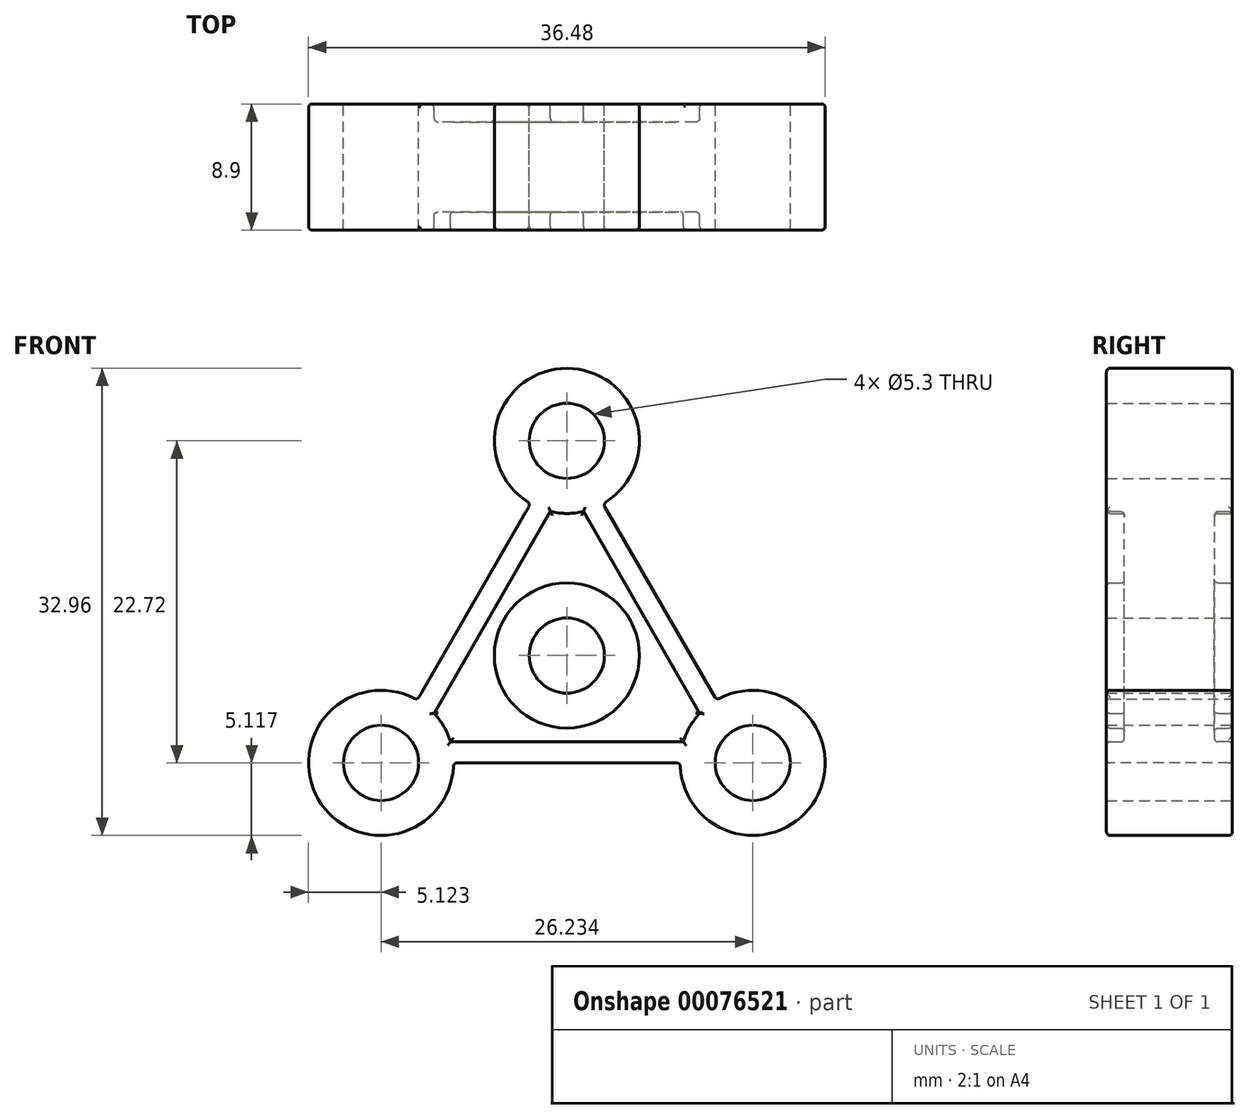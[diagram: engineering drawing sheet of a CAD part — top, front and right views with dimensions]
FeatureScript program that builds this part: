
annotation { "Feature Type Name" : "Feature", "Feature Type Description" : "" }
export const myFeature = defineFeature(function(context is Context, id is Id, definition is map)
    precondition{}
    {
        {
            var Q0;
            Q0=qCreatedBy(makeId("Front.planeOp"),FACE);
            var sketch = newSketch(context, id + "F0", { "sketchPlane" : qUnion([Q0])});
            skCircle(sketch, "E0.cCircle", {"center": v(0, 0) * mm, "radius": 7.57 * mm, "construction": true});
            skLineSegment(sketch, "E0.0", {"start": v(12.23, -7.57) * mm, "end": v(-12.23, -7.57) * mm});
            skLineSegment(sketch, "E0.1", {"start": v(-12.67, -6.8) * mm, "end": v(-0.44, 14.38) * mm});
            skLineSegment(sketch, "E0.2", {"start": v(0.44, 14.38) * mm, "end": v(12.67, -6.8) * mm});
            skPoint(sketch, "E0.0.midPoint", {"position": v(0, -7.57) * mm});
            skLineSegment(sketch, "E1", {"start": v(-0.44, 14.38) * mm, "end": v(0.44, 14.38) * mm});
            skLineSegment(sketch, "E2", {"start": v(12.67, -6.8) * mm, "end": v(12.23, -7.57) * mm});
            skLineSegment(sketch, "E3", {"start": v(-12.23, -7.57) * mm, "end": v(-12.67, -6.8) * mm});
            skPoint(sketch, "E4.orphan", {"position": v(0, 15.15) * mm});
            skPoint(sketch, "E5.orphan", {"position": v(-13.12, -7.57) * mm});
            skPoint(sketch, "E6.orphan", {"position": v(13.12, -7.57) * mm});
            skLineSegment(sketch, "E7", {"start": v(0, 0) * mm, "end": v(13.12, -7.57) * mm, "construction": true});
            skLineSegment(sketch, "E8", {"start": v(0, 0) * mm, "end": v(0, 15.15) * mm, "construction": true});
            skLineSegment(sketch, "E9", {"start": v(0, 0) * mm, "end": v(-13.12, -7.57) * mm, "construction": true});
            skSolve(sketch);
        }
        {
            var Q0;
            Q0=qCreatedBy(makeId("Front.planeOp"),FACE);
            var sketch = newSketch(context, id + "F2", { "sketchPlane" : qUnion([Q0])});
            skLineSegment(sketch, "E10.0.0", {"start": v(-12.23, -7.57) * mm, "end": v(12.23, -7.57) * mm});
            skLineSegment(sketch, "E10.0.1", {"start": v(12.23, -7.57) * mm, "end": v(12.67, -6.8) * mm});
            skLineSegment(sketch, "E10.0.2", {"start": v(12.67, -6.8) * mm, "end": v(0.44, 14.38) * mm});
            skLineSegment(sketch, "E10.0.3", {"start": v(0.44, 14.38) * mm, "end": v(-0.44, 14.38) * mm});
            skLineSegment(sketch, "E10.0.4", {"start": v(-0.44, 14.38) * mm, "end": v(-12.67, -6.8) * mm});
            skLineSegment(sketch, "E10.0.5", {"start": v(-12.67, -6.8) * mm, "end": v(-12.23, -7.57) * mm});
            skPoint(sketch, "E11.0", {"position": v(0, 0) * mm});
            skPoint(sketch, "E12.0", {"position": v(0, 15.15) * mm});
            skPoint(sketch, "E13.0", {"position": v(-13.12, -7.57) * mm});
            skPoint(sketch, "E14.0", {"position": v(13.12, -7.57) * mm});
            skPoint(sketch, "E15.0", {"position": v(0, -7.57) * mm});
            skCircle(sketch, "E16", {"center": v(0, 15.15) * mm, "radius": 5.12 * mm});
            skCircle(sketch, "E17", {"center": v(-13.12, -7.57) * mm, "radius": 5.12 * mm});
            skCircle(sketch, "E18", {"center": v(13.12, -7.57) * mm, "radius": 5.12 * mm});
            skCircle(sketch, "E19", {"center": v(0, 0) * mm, "radius": 2.65 * mm});
            skCircle(sketch, "E20", {"center": v(13.12, -7.57) * mm, "radius": 2.65 * mm});
            skCircle(sketch, "E21", {"center": v(0, 15.15) * mm, "radius": 2.65 * mm});
            skCircle(sketch, "E22", {"center": v(-13.12, -7.57) * mm, "radius": 2.65 * mm});
            skCircle(sketch, "E23", {"center": v(0, 0) * mm, "radius": 5.12 * mm});
            skCircle(sketch, "E24.cCircle", {"center": v(0, 0) * mm, "radius": 6.09 * mm, "construction": true});
            skLineSegment(sketch, "E24.0", {"start": v(10.54, -6.09) * mm, "end": v(-10.54, -6.09) * mm});
            skLineSegment(sketch, "E24.1", {"start": v(-10.54, -6.09) * mm, "end": v(0, 12.17) * mm});
            skLineSegment(sketch, "E24.2", {"start": v(0, 12.17) * mm, "end": v(10.54, -6.09) * mm});
            skPoint(sketch, "E24.0.midPoint", {"position": v(0, -6.09) * mm});
            skSolve(sketch);
        }
        {
            var Q0;
            Q0 = qSketchRegion(id + "F2", true);
            var Q1;
            Q1=makeQuery(id+"F2.imprint","IMPRINT",FACE,{"disambiguationData":[TD([[makeQuery(id+"F2.imprint","IMPRINT",EDGE,{"derivedFrom":sQuery(id+"F2.wireOp",EDGE,"E19")}),-1.0]])]});
            var Q2;
            {var subQ0=sQuery(id+"F2.wireOp",EDGE,"E24.2");var subQ1=sQuery(id+"F2.wireOp",EDGE,"E18");var subQ2=makeQuery(id+"F2.imprint","INTERSECT",VERTEX,{"derivedFrom":[subQ1,subQ0]});Q2=makeQuery(id+"F2.imprint","IMPRINT",FACE,{"disambiguationData":[TD([[makeQuery(id+"F2.imprint","IMPRINT",EDGE,{"disambiguationData":[TD([[subQ2,-1.0]])],"derivedFrom":subQ1}),1.0]])]});}
            var Q3;
            {var subQ0=sQuery(id+"F2.wireOp",EDGE,"E24.1");var subQ1=sQuery(id+"F2.wireOp",EDGE,"E16");var subQ2=makeQuery(id+"F2.imprint","INTERSECT",VERTEX,{"derivedFrom":[subQ1,subQ0]});Q3=makeQuery(id+"F2.imprint","IMPRINT",FACE,{"disambiguationData":[TD([[makeQuery(id+"F2.imprint","IMPRINT",EDGE,{"disambiguationData":[TD([[subQ2,-1.0]])],"derivedFrom":subQ1}),1.0]])]});}
            var Q4;
            Q4=makeQuery(id+"F2.imprint","IMPRINT",FACE,{"disambiguationData":[TD([[makeQuery(id+"F2.imprint","IMPRINT",EDGE,{"derivedFrom":sQuery(id+"F2.wireOp",EDGE,"E23")}),-1.0]])]});
            var Q5;
            {var subQ0=sQuery(id+"F2.wireOp",EDGE,"E24.0");var subQ1=sQuery(id+"F2.wireOp",EDGE,"E17");var subQ2=makeQuery(id+"F2.imprint","INTERSECT",VERTEX,{"derivedFrom":[subQ1,subQ0]});Q5=makeQuery(id+"F2.imprint","IMPRINT",FACE,{"disambiguationData":[TD([[makeQuery(id+"F2.imprint","IMPRINT",EDGE,{"disambiguationData":[TD([[subQ2,-1.0]])],"derivedFrom":subQ1}),1.0]])]});}
            extrude(context, id + "F3", {"entities" : qUnion([Q0, Q1, Q2, Q3, Q4, Q5]), "endBound" : BoundingType.SYMMETRIC, "depth" : 6.35 * mm});
        }
        {
            var Q0;
            {var subQ0=sQuery(id+"F2.wireOp",EDGE,"E18");var subQ1=sQuery(id+"F2.wireOp",EDGE,"E10.0.0");var subQ2=makeQuery(id+"F2.imprint","INTERSECT",VERTEX,{"derivedFrom":[subQ1,subQ0]});Q0=makeQuery(id+"F2.imprint","IMPRINT",FACE,{"disambiguationData":[TD([[makeQuery(id+"F2.imprint","IMPRINT",EDGE,{"disambiguationData":[TD([[subQ2,-1.0]])],"derivedFrom":subQ1}),-1.0]])]});}
            var Q1;
            {var subQ0=sQuery(id+"F2.wireOp",EDGE,"E18");var subQ1=sQuery(id+"F2.wireOp",EDGE,"E10.0.0");var subQ2=makeQuery(id+"F2.imprint","INTERSECT",VERTEX,{"derivedFrom":[subQ1,subQ0]});Q1=makeQuery(id+"F2.imprint","IMPRINT",FACE,{"disambiguationData":[TD([[makeQuery(id+"F2.imprint","IMPRINT",EDGE,{"disambiguationData":[TD([[subQ2,-1.0]])],"derivedFrom":subQ1}),1.0]])]});}
            var Q2;
            {var subQ0=sQuery(id+"F2.wireOp",EDGE,"E16");var subQ1=sQuery(id+"F2.wireOp",EDGE,"E10.0.2");var subQ2=makeQuery(id+"F2.imprint","INTERSECT",VERTEX,{"derivedFrom":[subQ1,subQ0]});Q2=makeQuery(id+"F2.imprint","IMPRINT",FACE,{"disambiguationData":[TD([[makeQuery(id+"F2.imprint","IMPRINT",EDGE,{"disambiguationData":[TD([[subQ2,-1.0]])],"derivedFrom":subQ1}),-1.0]])]});}
            var Q3;
            {var subQ0=sQuery(id+"F2.wireOp",EDGE,"E16");var subQ1=sQuery(id+"F2.wireOp",EDGE,"E10.0.2");var subQ2=makeQuery(id+"F2.imprint","INTERSECT",VERTEX,{"derivedFrom":[subQ1,subQ0]});Q3=makeQuery(id+"F2.imprint","IMPRINT",FACE,{"disambiguationData":[TD([[makeQuery(id+"F2.imprint","IMPRINT",EDGE,{"disambiguationData":[TD([[subQ2,-1.0]])],"derivedFrom":subQ1}),1.0]])]});}
            var Q4;
            {var subQ0=sQuery(id+"F2.wireOp",EDGE,"E17");var subQ1=sQuery(id+"F2.wireOp",EDGE,"E10.0.0");var subQ2=makeQuery(id+"F2.imprint","INTERSECT",VERTEX,{"derivedFrom":[subQ1,subQ0]});Q4=makeQuery(id+"F2.imprint","IMPRINT",FACE,{"disambiguationData":[TD([[makeQuery(id+"F2.imprint","IMPRINT",EDGE,{"disambiguationData":[TD([[subQ2,1.0]])],"derivedFrom":subQ1}),-1.0]])]});}
            var Q5;
            {var subQ0=sQuery(id+"F2.wireOp",EDGE,"E17");var subQ1=sQuery(id+"F2.wireOp",EDGE,"E10.0.0");var subQ2=makeQuery(id+"F2.imprint","INTERSECT",VERTEX,{"derivedFrom":[subQ1,subQ0]});Q5=makeQuery(id+"F2.imprint","IMPRINT",FACE,{"disambiguationData":[TD([[makeQuery(id+"F2.imprint","IMPRINT",EDGE,{"disambiguationData":[TD([[subQ2,1.0]])],"derivedFrom":subQ1}),1.0]])]});}
            var Q6;
            Q6=makeQuery(id+"F2.imprint","IMPRINT",FACE,{"disambiguationData":[TD([[makeQuery(id+"F2.imprint","IMPRINT",EDGE,{"derivedFrom":sQuery(id+"F2.wireOp",EDGE,"E19")}),-1.0]])]});
            var Q7;
            {var subQ0=sQuery(id+"F2.wireOp",EDGE,"E24.0");var subQ1=sQuery(id+"F2.wireOp",EDGE,"E17");var subQ2=makeQuery(id+"F2.imprint","INTERSECT",VERTEX,{"derivedFrom":[subQ1,subQ0]});Q7=makeQuery(id+"F2.imprint","IMPRINT",FACE,{"disambiguationData":[TD([[makeQuery(id+"F2.imprint","IMPRINT",EDGE,{"disambiguationData":[TD([[subQ2,-1.0]])],"derivedFrom":subQ1}),1.0]])]});}
            var Q8;
            {var subQ0=sQuery(id+"F2.wireOp",EDGE,"E24.2");var subQ1=sQuery(id+"F2.wireOp",EDGE,"E18");var subQ2=makeQuery(id+"F2.imprint","INTERSECT",VERTEX,{"derivedFrom":[subQ1,subQ0]});Q8=makeQuery(id+"F2.imprint","IMPRINT",FACE,{"disambiguationData":[TD([[makeQuery(id+"F2.imprint","IMPRINT",EDGE,{"disambiguationData":[TD([[subQ2,-1.0]])],"derivedFrom":subQ1}),1.0]])]});}
            var Q9;
            {var subQ0=sQuery(id+"F2.wireOp",EDGE,"E24.1");var subQ1=sQuery(id+"F2.wireOp",EDGE,"E16");var subQ2=makeQuery(id+"F2.imprint","INTERSECT",VERTEX,{"derivedFrom":[subQ1,subQ0]});Q9=makeQuery(id+"F2.imprint","IMPRINT",FACE,{"disambiguationData":[TD([[makeQuery(id+"F2.imprint","IMPRINT",EDGE,{"disambiguationData":[TD([[subQ2,-1.0]])],"derivedFrom":subQ1}),1.0]])]});}
            var Q10;
            {var subQ0=sQuery(id+"F2.wireOp",EDGE,"E16");var subQ1=sQuery(id+"F2.wireOp",EDGE,"E10.0.4");var subQ2=makeQuery(id+"F2.imprint","INTERSECT",VERTEX,{"derivedFrom":[subQ1,subQ0]});Q10=makeQuery(id+"F2.imprint","IMPRINT",FACE,{"disambiguationData":[TD([[makeQuery(id+"F2.imprint","IMPRINT",EDGE,{"disambiguationData":[TD([[subQ2,-1.0]])],"derivedFrom":subQ1}),1.0]])]});}
            var Q11;
            {var subQ0=sQuery(id+"F2.wireOp",EDGE,"E18");var subQ1=sQuery(id+"F2.wireOp",EDGE,"E10.0.2");var subQ2=makeQuery(id+"F2.imprint","INTERSECT",VERTEX,{"derivedFrom":[subQ1,subQ0]});Q11=makeQuery(id+"F2.imprint","IMPRINT",FACE,{"disambiguationData":[TD([[makeQuery(id+"F2.imprint","IMPRINT",EDGE,{"disambiguationData":[TD([[subQ2,-1.0]])],"derivedFrom":subQ1}),1.0]])]});}
            var Q12;
            {var subQ0=sQuery(id+"F2.wireOp",EDGE,"E17");var subQ1=sQuery(id+"F2.wireOp",EDGE,"E10.0.0");var subQ2=makeQuery(id+"F2.imprint","INTERSECT",VERTEX,{"derivedFrom":[subQ1,subQ0]});Q12=makeQuery(id+"F2.imprint","IMPRINT",FACE,{"disambiguationData":[TD([[makeQuery(id+"F2.imprint","IMPRINT",EDGE,{"disambiguationData":[TD([[subQ2,-1.0]])],"derivedFrom":subQ1}),1.0]])]});}
            extrude(context, id + "F1", {"entities" : qUnion([Q0, Q1, Q2, Q3, Q4, Q5, Q6, Q7, Q8, Q9, Q10, Q11, Q12]), "operationType" : NewBodyOperationType.ADD, "endBound" : BoundingType.SYMMETRIC, "depth" : 8.9 * mm});
        }
        {
            var Q0;
            Q0=makeQuery(id+"F1.opExtrude","CAP_EDGE",EDGE,{"disambiguationData":[OSD([sQuery(id+"F2.wireOp",EDGE,"E24.1")])],"isStart":false});
            var Q1;
            Q1=makeQuery(id+"F1.opExtrude","CAP_EDGE",EDGE,{"disambiguationData":[OSD([sQuery(id+"F2.wireOp",EDGE,"E24.2")])],"isStart":false});
            var Q2;
            {var subQ0=sQuery(id+"F2.wireOp",EDGE,"E16");Q2=makeQuery(id+"F1.opExtrude","CAP_EDGE",EDGE,{"disambiguationData":[OSD([subQ0]),TDD([makeQuery(id+"F2.imprint","IMPRINT",EDGE,{"disambiguationData":[TD([[makeQuery(id+"F2.imprint","INTERSECT",VERTEX,{"derivedFrom":[subQ0,sQuery(id+"F2.wireOp",EDGE,"E24.1")]}),-1.0]])],"derivedFrom":subQ0})])],"isStart":false});}
            var Q3;
            Q3=makeQuery(id+"F1.opExtrude","CAP_EDGE",EDGE,{"disambiguationData":[OSD([sQuery(id+"F2.wireOp",EDGE,"E24.0")])],"isStart":false});
            var Q4;
            {var subQ0=sQuery(id+"F2.wireOp",EDGE,"E18");Q4=makeQuery(id+"F1.opExtrude","CAP_EDGE",EDGE,{"disambiguationData":[OSD([subQ0]),TDD([makeQuery(id+"F2.imprint","IMPRINT",EDGE,{"disambiguationData":[TD([[makeQuery(id+"F2.imprint","INTERSECT",VERTEX,{"derivedFrom":[subQ0,sQuery(id+"F2.wireOp",EDGE,"E24.2")]}),-1.0]])],"derivedFrom":subQ0})])],"isStart":false});}
            var Q5;
            {var subQ0=sQuery(id+"F2.wireOp",EDGE,"E17");Q5=makeQuery(id+"F1.opExtrude","CAP_EDGE",EDGE,{"disambiguationData":[OSD([subQ0]),TDD([makeQuery(id+"F2.imprint","IMPRINT",EDGE,{"disambiguationData":[TD([[makeQuery(id+"F2.imprint","INTERSECT",VERTEX,{"derivedFrom":[subQ0,sQuery(id+"F2.wireOp",EDGE,"E24.0")]}),-1.0]])],"derivedFrom":subQ0})])],"isStart":false});}
            var Q6;
            Q6=makeQuery(id+"F1.opExtrude","CAP_EDGE",EDGE,{"disambiguationData":[OSD([sQuery(id+"F2.wireOp",EDGE,"E23")])],"isStart":false});
            var Q7;
            Q7=makeQuery(id+"F3.opExtrude","CAP_FACE",FACE,{"disambiguationData":[OSD([sQuery(id+"F2.wireOp",EDGE,"E10.0.0"),sQuery(id+"F2.wireOp",EDGE,"E10.0.2"),sQuery(id+"F2.wireOp",EDGE,"E10.0.4"),sQuery(id+"F2.wireOp",EDGE,"E16"),sQuery(id+"F2.wireOp",EDGE,"E17"),sQuery(id+"F2.wireOp",EDGE,"E18"),sQuery(id+"F2.wireOp",EDGE,"E19"),sQuery(id+"F2.wireOp",EDGE,"E20"),sQuery(id+"F2.wireOp",EDGE,"E21"),sQuery(id+"F2.wireOp",EDGE,"E22")])],"isStart":false});
            var Q8;
            {var subQ0=sQuery(id+"F2.wireOp",EDGE,"E17");Q8=makeQuery(id+"F1.boolean.opBoolean","MERGE",FACE,{"derivedFrom":[makeQuery(id+"F3.opExtrude","SWEPT_FACE",FACE,{"disambiguationData":[OSD([subQ0])]}),makeQuery(id+"F1.opExtrude","SWEPT_FACE",FACE,{"disambiguationData":[OSD([subQ0]),TDD([makeQuery(id+"F2.imprint","IMPRINT",EDGE,{"disambiguationData":[TD([[makeQuery(id+"F2.imprint","INTERSECT",VERTEX,{"derivedFrom":[sQuery(id+"F2.wireOp",EDGE,"E10.0.0"),subQ0]}),1.0]])],"derivedFrom":subQ0})])]})]});}
            var Q9;
            {var subQ0=sQuery(id+"F2.wireOp",EDGE,"E16");Q9=makeQuery(id+"F1.opExtrude","CAP_EDGE",EDGE,{"disambiguationData":[OSD([subQ0]),TDD([makeQuery(id+"F2.imprint","IMPRINT",EDGE,{"disambiguationData":[TD([[makeQuery(id+"F2.imprint","INTERSECT",VERTEX,{"derivedFrom":[sQuery(id+"F2.wireOp",EDGE,"E10.0.2"),subQ0]}),-1.0]])],"derivedFrom":subQ0})])],"isStart":true});}
            var Q10;
            Q10=makeQuery(id+"F1.opExtrude","CAP_EDGE",EDGE,{"disambiguationData":[OSD([sQuery(id+"F2.wireOp",EDGE,"E23")])],"isStart":true});
            var Q11;
            Q11=makeQuery(id+"F1.opExtrude","CAP_EDGE",EDGE,{"disambiguationData":[OSD([sQuery(id+"F2.wireOp",EDGE,"E10.0.2")])],"isStart":true});
            var Q12;
            Q12=makeQuery(id+"F1.boolean.opBoolean","INTERSECT",EDGE,{"derivedFrom":[makeQuery(id+"F3.opExtrude","CAP_FACE",FACE,{"disambiguationData":[OSD([sQuery(id+"F2.wireOp",EDGE,"E10.0.0"),sQuery(id+"F2.wireOp",EDGE,"E10.0.2"),sQuery(id+"F2.wireOp",EDGE,"E10.0.4"),sQuery(id+"F2.wireOp",EDGE,"E16"),sQuery(id+"F2.wireOp",EDGE,"E17"),sQuery(id+"F2.wireOp",EDGE,"E18"),sQuery(id+"F2.wireOp",EDGE,"E19"),sQuery(id+"F2.wireOp",EDGE,"E20"),sQuery(id+"F2.wireOp",EDGE,"E21"),sQuery(id+"F2.wireOp",EDGE,"E22")])],"isStart":true}),makeQuery(id+"F1.opExtrude","SWEPT_FACE",FACE,{"disambiguationData":[OSD([sQuery(id+"F2.wireOp",EDGE,"E23")])]})]});
            var Q13;
            Q13=makeQuery(id+"F1.opExtrude","CAP_EDGE",EDGE,{"disambiguationData":[OSD([sQuery(id+"F2.wireOp",EDGE,"E24.2")])],"isStart":true});
            var Q14;
            Q14=makeQuery(id+"F1.opExtrude","CAP_EDGE",EDGE,{"disambiguationData":[OSD([sQuery(id+"F2.wireOp",EDGE,"E24.1")])],"isStart":true});
            var Q15;
            {var subQ0=sQuery(id+"F2.wireOp",EDGE,"E16");Q15=makeQuery(id+"F1.opExtrude","CAP_EDGE",EDGE,{"disambiguationData":[OSD([subQ0]),TDD([makeQuery(id+"F2.imprint","IMPRINT",EDGE,{"disambiguationData":[TD([[makeQuery(id+"F2.imprint","INTERSECT",VERTEX,{"derivedFrom":[subQ0,sQuery(id+"F2.wireOp",EDGE,"E24.1")]}),-1.0]])],"derivedFrom":subQ0})])],"isStart":true});}
            var Q16;
            Q16=makeQuery(id+"F3.opExtrude","CAP_FACE",FACE,{"disambiguationData":[OSD([sQuery(id+"F2.wireOp",EDGE,"E10.0.0"),sQuery(id+"F2.wireOp",EDGE,"E10.0.2"),sQuery(id+"F2.wireOp",EDGE,"E10.0.4"),sQuery(id+"F2.wireOp",EDGE,"E16"),sQuery(id+"F2.wireOp",EDGE,"E17"),sQuery(id+"F2.wireOp",EDGE,"E18"),sQuery(id+"F2.wireOp",EDGE,"E19"),sQuery(id+"F2.wireOp",EDGE,"E20"),sQuery(id+"F2.wireOp",EDGE,"E21"),sQuery(id+"F2.wireOp",EDGE,"E22")])],"isStart":true});
            var Q17;
            {var subQ0=sQuery(id+"F2.wireOp",EDGE,"E18");Q17=makeQuery(id+"F1.opExtrude","CAP_EDGE",EDGE,{"disambiguationData":[OSD([subQ0]),TDD([makeQuery(id+"F2.imprint","IMPRINT",EDGE,{"disambiguationData":[TD([[makeQuery(id+"F2.imprint","INTERSECT",VERTEX,{"derivedFrom":[sQuery(id+"F2.wireOp",EDGE,"E10.0.0"),subQ0]}),-1.0]])],"derivedFrom":subQ0})])],"isStart":true});}
            var Q18;
            {var subQ0=sQuery(id+"F2.wireOp",EDGE,"E16");Q18=makeQuery(id+"F1.opExtrude","CAP_EDGE",EDGE,{"disambiguationData":[OSD([subQ0]),TDD([makeQuery(id+"F2.imprint","IMPRINT",EDGE,{"disambiguationData":[TD([[makeQuery(id+"F2.imprint","INTERSECT",VERTEX,{"derivedFrom":[sQuery(id+"F2.wireOp",EDGE,"E10.0.2"),subQ0]}),-1.0]])],"derivedFrom":subQ0})])],"isStart":false});}
            var Q19;
            {var subQ0=sQuery(id+"F2.wireOp",EDGE,"E18");Q19=makeQuery(id+"F1.opExtrude","CAP_EDGE",EDGE,{"disambiguationData":[OSD([subQ0]),TDD([makeQuery(id+"F2.imprint","IMPRINT",EDGE,{"disambiguationData":[TD([[makeQuery(id+"F2.imprint","INTERSECT",VERTEX,{"derivedFrom":[sQuery(id+"F2.wireOp",EDGE,"E10.0.0"),subQ0]}),-1.0]])],"derivedFrom":subQ0})])],"isStart":false});}
            var Q20;
            Q20=makeQuery(id+"F1.opExtrude","CAP_EDGE",EDGE,{"disambiguationData":[OSD([sQuery(id+"F2.wireOp",EDGE,"E10.0.2")])],"isStart":false});
            var Q21;
            {var subQ0=sQuery(id+"F2.wireOp",EDGE,"E17");Q21=makeQuery(id+"F1.opExtrude","CAP_EDGE",EDGE,{"disambiguationData":[OSD([subQ0]),TDD([makeQuery(id+"F2.imprint","IMPRINT",EDGE,{"disambiguationData":[TD([[makeQuery(id+"F2.imprint","INTERSECT",VERTEX,{"derivedFrom":[subQ0,sQuery(id+"F2.wireOp",EDGE,"E24.0")]}),-1.0]])],"derivedFrom":subQ0})])],"isStart":true});}
            var Q22;
            {var subQ0=sQuery(id+"F2.wireOp",EDGE,"E22");var subQ1=sQuery(id+"F2.wireOp",EDGE,"E21");var subQ2=sQuery(id+"F2.wireOp",EDGE,"E20");var subQ3=sQuery(id+"F2.wireOp",EDGE,"E18");var subQ4=sQuery(id+"F2.wireOp",EDGE,"E17");var subQ5=sQuery(id+"F2.wireOp",EDGE,"E16");var subQ6=sQuery(id+"F2.wireOp",EDGE,"E10.0.4");var subQ7=sQuery(id+"F2.wireOp",EDGE,"E10.0.2");var subQ8=sQuery(id+"F2.wireOp",EDGE,"E10.0.0");var subQ11=sQuery(id+"F2.wireOp",EDGE,"E24.0");Q22=makeQuery(id+"F1.boolean.opBoolean","SPLIT",FACE,{"disambiguationData":[TD([makeQuery(id+"F3.opExtrude","CAP_FACE",FACE,{"disambiguationData":[OSD([subQ8,subQ7,subQ6,subQ5,subQ4,subQ3,sQuery(id+"F2.wireOp",EDGE,"E19"),subQ2,subQ1,subQ0])],"isStart":true})])],"derivedFrom":makeQuery(id+"F1.opExtrude","SWEPT_FACE",FACE,{"disambiguationData":[OSD([subQ11])]})});}
            var Q23;
            {var subQ0=sQuery(id+"F2.wireOp",EDGE,"E10.0.0");Q23=makeQuery(id+"F1.boolean.opBoolean","MERGE",FACE,{"derivedFrom":[makeQuery(id+"F3.opExtrude","SWEPT_FACE",FACE,{"disambiguationData":[OSD([subQ0])]}),makeQuery(id+"F1.opExtrude","SWEPT_FACE",FACE,{"disambiguationData":[OSD([subQ0])]})]});}
            var Q24;
            {var subQ0=sQuery(id+"F2.wireOp",EDGE,"E10.0.2");Q24=makeQuery(id+"F1.boolean.opBoolean","MERGE",FACE,{"derivedFrom":[makeQuery(id+"F3.opExtrude","SWEPT_FACE",FACE,{"disambiguationData":[OSD([subQ0])]}),makeQuery(id+"F1.opExtrude","SWEPT_FACE",FACE,{"disambiguationData":[OSD([subQ0])]})]});}
            var Q25;
            {var subQ0=sQuery(id+"F2.wireOp",EDGE,"E16");var subQ1=sQuery(id+"F2.wireOp",EDGE,"E10.0.4");Q25=makeQuery(id+"F1.boolean.opBoolean","MERGE",EDGE,{"derivedFrom":[makeQuery(id+"F3.opExtrude","SWEPT_EDGE",EDGE,{"disambiguationData":[OSD([subQ1,subQ0])]}),makeQuery(id+"F1.opExtrude","SWEPT_EDGE",EDGE,{"disambiguationData":[OSD([subQ1,subQ0])]})]});}
            fillet(context, id + "F4", {"entities" : qUnion([Q0, Q1, Q2, Q3, Q4, Q5, Q6, Q7, Q8, Q9, Q10, Q11, Q12, Q13, Q14, Q15, Q16, Q17, Q18, Q19, Q20, Q21, Q22, Q23, Q24, Q25]), "radius" : 0.25 * mm, "tangentPropagation" : true, "allowEdgeOverflow" : false});
        }
    });
